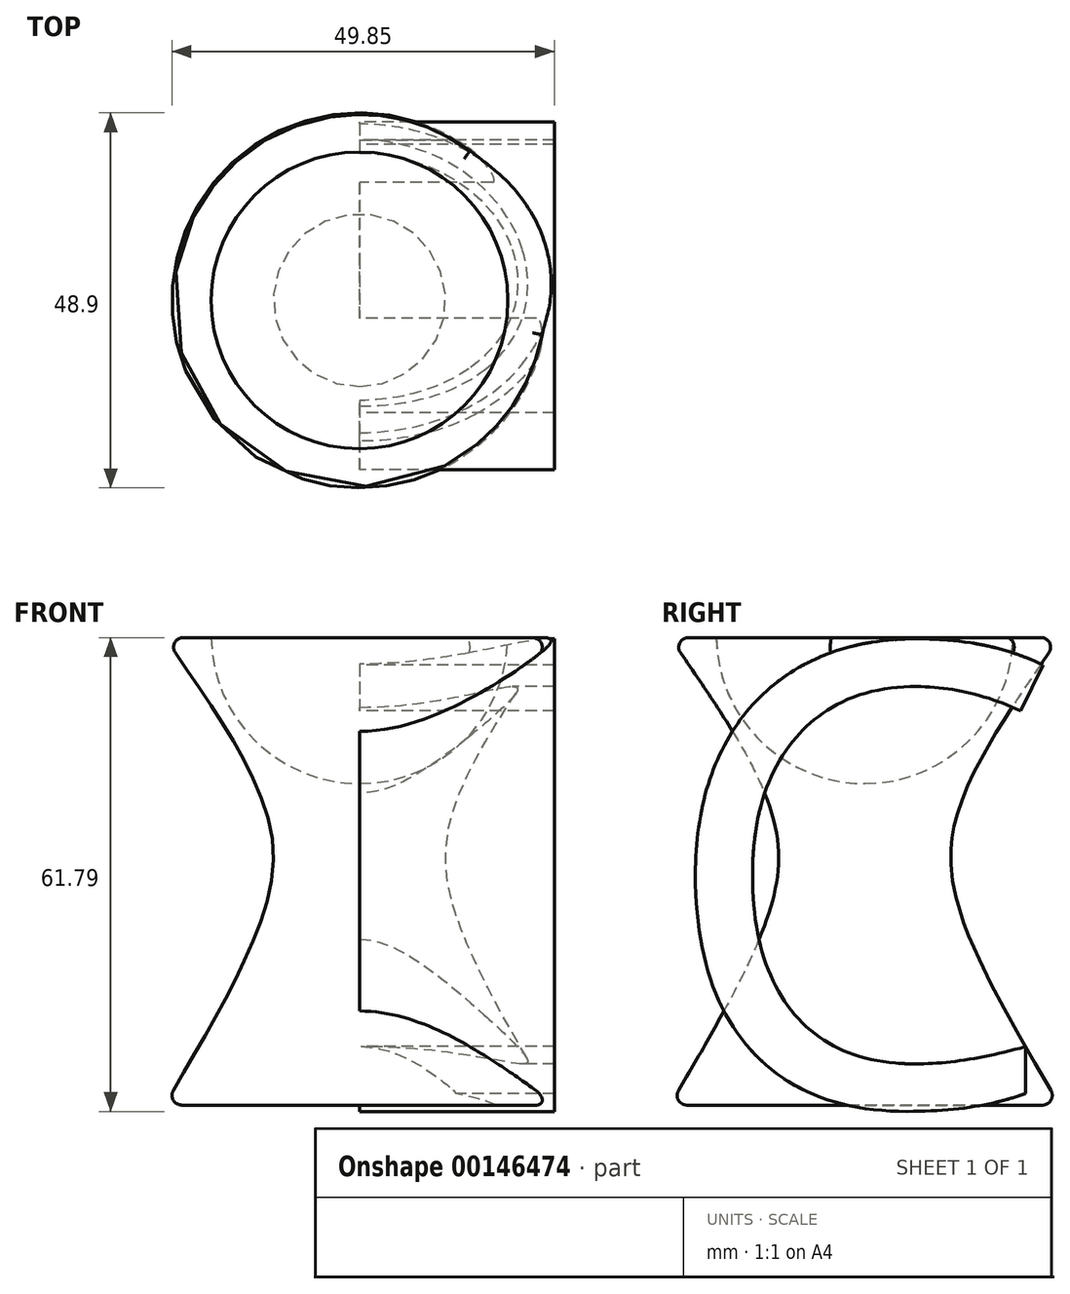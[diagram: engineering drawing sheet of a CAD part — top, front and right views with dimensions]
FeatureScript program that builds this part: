
annotation { "Feature Type Name" : "Feature", "Feature Type Description" : "" }
export const myFeature = defineFeature(function(context is Context, id is Id, definition is map)
    precondition{}
    {
        {
            var Q0;
            Q0=qCreatedBy(makeId("Top.planeOp"),FACE);
            var sketch = newSketch(context, id + "F0", { "sketchPlane" : qUnion([Q0])});
            skCircle(sketch, "E0", {"center": v(0, 0) * mm, "radius": 25.4 * mm});
            skSolve(sketch);
        }
        {
            var Q0;
            Q0=makeQuery(id+"F0.imprint","IMPRINT",FACE,{"disambiguationData":[TD([[makeQuery(id+"F0.imprint","IMPRINT",EDGE,{"derivedFrom":sQuery(id+"F0.wireOp",EDGE,"E0")}),1.0]])]});
            extrude(context, id + "F1", {"entities" : qUnion([Q0]), "depth" : 60.96 * mm});
        }
        {
            var Q0;
            Q0=qCreatedBy(makeId("Front.planeOp"),FACE);
            var sketch = newSketch(context, id + "F2", { "sketchPlane" : qUnion([Q0])});
            skLineSegment(sketch, "E1", {"start": v(-25.4, 69.33) * mm, "end": v(-25.4, -16.73) * mm});
            skLineSegment(sketch, "E2", {"start": v(0, 72.75) * mm, "end": v(0, -27.61) * mm, "construction": true});
            skLineSegment(sketch, "E3", {"start": v(-58.45, 60.96) * mm, "end": v(39.5, 60.96) * mm, "construction": true});
            skFitSpline(sketch, "E4", {"points": [v(-25.4, 60.96) * mm, v(-11.9, 37.28) * mm, v(-13.3, 22.77) * mm, v(-25.4, 0) * mm], "startDerivative": vector(47.31, -67.78) * mm, "endDerivative": vector(-39.5, -66.85) * mm});
            skLineSegment(sketch, "E5", {"start": v(-25.4, 60.96) * mm, "end": v(-25.4, 0) * mm});
            skSolve(sketch);
        }
        {
            var Q0;
            Q0 = qSketchRegion(id + "F2", true);
            var Q1;
            Q1=sQuery(id+"F2.wireOp",EDGE,"E2");
            revolve(context, id + "F3", {"operationType" : NewBodyOperationType.REMOVE, "entities" : qUnion([Q0]), "axis" : qUnion([Q1]), "revolveType" : RevolveType.FULL, "oppositeDirection" : true});
        }
        {
            var Q0;
            Q0=qCreatedBy(makeId("Right.planeOp"),FACE);
            var sketch = newSketch(context, id + "F4", { "sketchPlane" : qUnion([Q0])});
            skText(sketch, "E6", { "text": "C", "fontName": "OpenSans-Regular.ttf"});
            const initialGuessF4  = {"E6": [-0.0272, 0, 1, 0, 0.06046]};
            skSetInitialGuess(sketch, initialGuessF4);
            skSolve(sketch);
        }
        {
            var Q0;
            Q0 = qSketchRegion(id + "F4", true);
            extrude(context, id + "F5", {"entities" : qUnion([Q0]), "operationType" : NewBodyOperationType.ADD, "depth" : 25.4 * mm});
        }
        {
            var Q0;
            Q0=qCreatedBy(makeId("Right.planeOp"),FACE);
            var sketch = newSketch(context, id + "F6", { "sketchPlane" : qUnion([Q0])});
            skArc(sketch, "E7", {"start": v(0, 41.92) * mm, "mid": v(19.35, 61.27) * mm, "end": v(0, 80.61) * mm});
            skLineSegment(sketch, "E8", {"start": v(0, 80.61) * mm, "end": v(0, 41.92) * mm});
            skSolve(sketch);
        }
        {
            var Q0;
            Q0 = qSketchRegion(id + "F6", true);
            var Q1;
            Q1=sQuery(id+"F6.wireOp",EDGE,"E8");
            revolve(context, id + "F7", {"operationType" : NewBodyOperationType.REMOVE, "entities" : qUnion([Q0]), "axis" : qUnion([Q1]), "revolveType" : RevolveType.FULL, "oppositeDirection" : true});
        }
        {
            var Q0;
            {var subQ0=sQuery(id+"F2.wireOp",EDGE,"E5");var subQ1=sQuery(id+"F2.wireOp",EDGE,"E4");Q0=makeQuery(id+"F3.boolean.opBoolean","MERGE",EDGE,{"derivedFrom":[makeQuery(id+"F1.opExtrude","CAP_EDGE",EDGE,{"disambiguationData":[OSD([sQuery(id+"F0.wireOp",EDGE,"E0")])],"isStart":false}),makeQuery(id+"F3.opRevolve","SWEPT_EDGE",EDGE,{"disambiguationData":[OSD([subQ1,subQ0]),TDD([makeQuery(id+"F2.imprint","INTERSECT",VERTEX,{"disambiguationData":[OD(0.0)],"derivedFrom":[subQ1,subQ0]})])]})]});}
            var Q1;
            {var subQ0=sQuery(id+"F2.wireOp",EDGE,"E5");var subQ1=sQuery(id+"F2.wireOp",EDGE,"E4");Q1=makeQuery(id+"F3.boolean.opBoolean","MERGE",EDGE,{"derivedFrom":[makeQuery(id+"F1.opExtrude","CAP_EDGE",EDGE,{"disambiguationData":[OSD([sQuery(id+"F0.wireOp",EDGE,"E0")])],"isStart":true}),makeQuery(id+"F3.opRevolve","SWEPT_EDGE",EDGE,{"disambiguationData":[OSD([subQ1,subQ0]),TDD([makeQuery(id+"F2.imprint","INTERSECT",VERTEX,{"disambiguationData":[OD(1.0)],"derivedFrom":[subQ1,subQ0]})])]})]});}
            fillet(context, id + "F8", {"entities" : qUnion([Q0, Q1]), "radius" : 1.27 * mm, "allowEdgeOverflow" : false});
        }
    });
